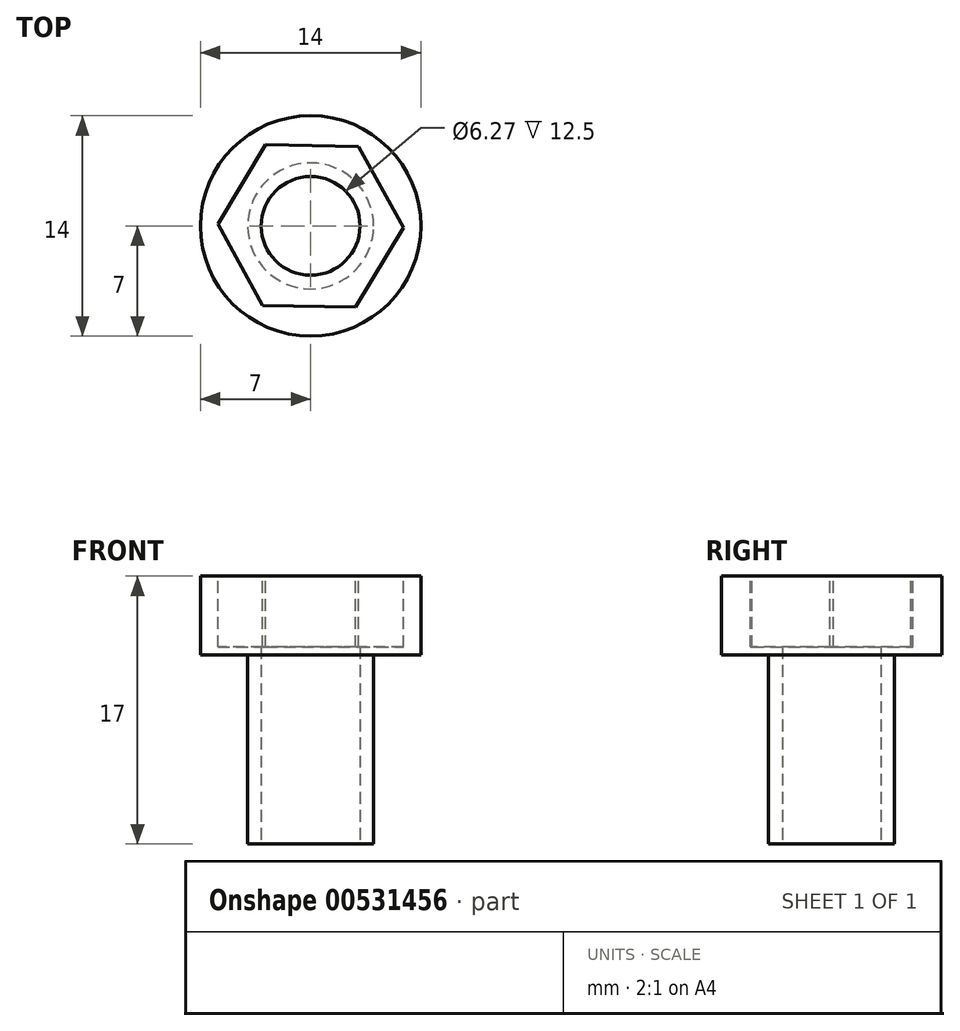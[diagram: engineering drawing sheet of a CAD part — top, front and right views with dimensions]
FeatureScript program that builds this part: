
annotation { "Feature Type Name" : "Feature", "Feature Type Description" : "" }
export const myFeature = defineFeature(function(context is Context, id is Id, definition is map)
    precondition{}
    {
        {
            var Q0;
            Q0=qCreatedBy(makeId("Top.planeOp"),FACE);
            var sketch = newSketch(context, id + "F0", { "sketchPlane" : qUnion([Q0])});
            skCircle(sketch, "E0", {"center": v(0, 0) * mm, "radius": 4 * mm});
            skSolve(sketch);
        }
        {
            var Q0;
            Q0 = qSketchRegion(id + "F0", true);
            extrude(context, id + "F1", {"entities" : qUnion([Q0]), "depth" : 12 * mm, "offsetDistance" : 25 * mm});
        }
        {
            var Q0;
            Q0=makeQuery(id+"F1.opExtrude","CAP_FACE",FACE,{"disambiguationData":[OSD([sQuery(id+"F0.wireOp",EDGE,"k386WdcR-Rpl0-2yvB-Ydco-ZqtedZE1ulTk"),sQuery(id+"F0.wireOp",EDGE,"E0")])],"isStart":false});
            var sketch = newSketch(context, id + "F2", { "sketchPlane" : qUnion([Q0])});
            skCircle(sketch, "E1", {"center": v(0, 0) * mm, "radius": 7 * mm});
            skSolve(sketch);
        }
        {
            var Q0;
            Q0 = qSketchRegion(id + "F2", true);
            extrude(context, id + "F3", {"entities" : qUnion([Q0]), "operationType" : NewBodyOperationType.ADD, "depth" : 5 * mm, "offsetDistance" : 25 * mm});
        }
        {
            var Q0;
            Q0=makeQuery(id+"F3.opExtrude","CAP_FACE",FACE,{"disambiguationData":[OSD([sQuery(id+"F2.wireOp",EDGE,"E1")])],"isStart":false});
            var sketch = newSketch(context, id + "F4", { "sketchPlane" : qUnion([Q0])});
            skCircle(sketch, "E2.cCircle", {"center": v(0, 0) * mm, "radius": 5.1 * mm, "construction": true});
            skLineSegment(sketch, "E2.0", {"start": v(3.04, 5.05) * mm, "end": v(5.89, -0.1) * mm});
            skLineSegment(sketch, "E2.1", {"start": v(5.89, -0.1) * mm, "end": v(2.85, -5.15) * mm});
            skLineSegment(sketch, "E2.2", {"start": v(2.85, -5.15) * mm, "end": v(-3.04, -5.05) * mm});
            skLineSegment(sketch, "E2.3", {"start": v(-3.04, -5.05) * mm, "end": v(-5.89, 0.1) * mm});
            skLineSegment(sketch, "E2.4", {"start": v(-5.89, 0.1) * mm, "end": v(-2.85, 5.15) * mm});
            skLineSegment(sketch, "E2.5", {"start": v(-2.85, 5.15) * mm, "end": v(3.04, 5.05) * mm});
            skPoint(sketch, "E2.0.midPoint", {"position": v(4.46, 2.47) * mm});
            skSolve(sketch);
        }
        {
            var Q0;
            Q0=makeQuery(id+"F4.imprint","IMPRINT",FACE,{"disambiguationData":[TD([[makeQuery(id+"F4.imprint","IMPRINT",EDGE,{"derivedFrom":sQuery(id+"F4.wireOp",EDGE,"E2.0")}),-1.0]])]});
            extrude(context, id + "F5", {"entities" : qUnion([Q0]), "operationType" : NewBodyOperationType.REMOVE, "oppositeDirection" : true, "depth" : 4.5 * mm, "offsetDistance" : 25 * mm});
        }
        {
            var Q0;
            Q0=makeQuery(id+"F1.opExtrude","CAP_FACE",FACE,{"disambiguationData":[OSD([sQuery(id+"F0.wireOp",EDGE,"E0")])],"isStart":true});
            var sketch = newSketch(context, id + "F6", { "sketchPlane" : qUnion([Q0])});
            skCircle(sketch, "E3", {"center": v(0, 0) * mm, "radius": 3.14 * mm});
            skSolve(sketch);
        }
        {
            var Q0;
            Q0 = qSketchRegion(id + "F6", true);
            extrude(context, id + "F7", {"entities" : qUnion([Q0]), "operationType" : NewBodyOperationType.REMOVE, "oppositeDirection" : true, "depth" : 25 * mm, "offsetDistance" : 25 * mm});
        }
    });
